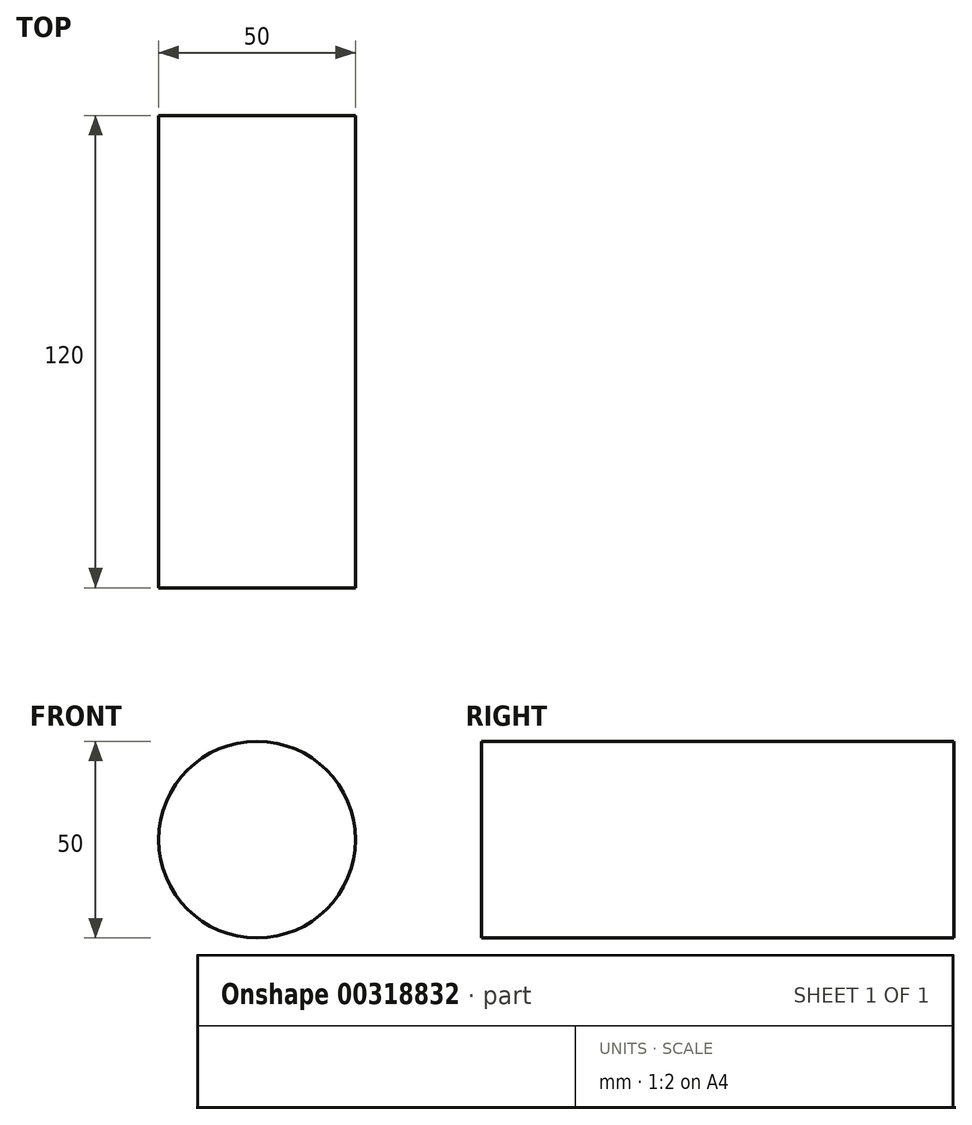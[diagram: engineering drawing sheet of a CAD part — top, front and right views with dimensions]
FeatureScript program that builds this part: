
annotation { "Feature Type Name" : "Feature", "Feature Type Description" : "" }
export const myFeature = defineFeature(function(context is Context, id is Id, definition is map)
    precondition{}
    {
        {
            var Q0;
            Q0=qCreatedBy(makeId("Front.planeOp"),FACE);
            var sketch = newSketch(context, id + "F0", { "sketchPlane" : qUnion([Q0])});
            skCircle(sketch, "E0", {"center": v(16.2, 19.05) * mm, "radius": 25 * mm});
            skSolve(sketch);
        }
        {
            var Q0;
            Q0=makeQuery(id+"F0.imprint","IMPRINT",FACE,{"disambiguationData":[TD([[makeQuery(id+"F0.imprint","IMPRINT",EDGE,{"derivedFrom":sQuery(id+"F0.wireOp",EDGE,"E0")}),1.0]])]});
            extrude(context, id + "F1", {"entities" : qUnion([Q0]), "depth" : 120 * mm});
        }
    });
